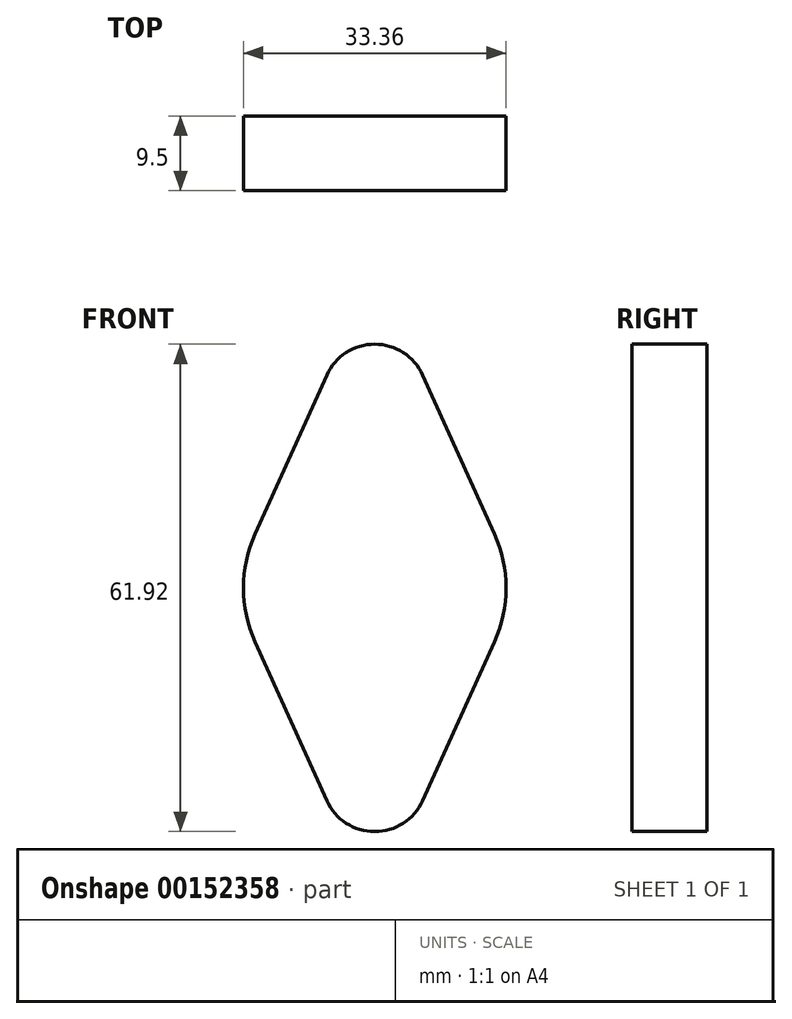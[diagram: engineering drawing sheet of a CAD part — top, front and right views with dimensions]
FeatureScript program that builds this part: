
annotation { "Feature Type Name" : "Feature", "Feature Type Description" : "" }
export const myFeature = defineFeature(function(context is Context, id is Id, definition is map)
    precondition{}
    {
        {
            var Q0;
            Q0=qCreatedBy(makeId("Front.planeOp"),FACE);
            var sketch = newSketch(context, id + "F0", { "sketchPlane" : qUnion([Q0])});
            skArc(sketch, "E0", {"start": v(6.09, 27.03) * mm, "mid": v(0, 30.96) * mm, "end": v(-6.09, 27.03) * mm});
            skArc(sketch, "E1.MirrorC", {"start": v(6.09, -27.03) * mm, "mid": v(0, -30.96) * mm, "end": v(-6.09, -27.03) * mm});
            skArc(sketch, "E2", {"start": v(-15.2, 6.86) * mm, "mid": v(-16.68, 0) * mm, "end": v(-15.2, -6.86) * mm});
            skLineSegment(sketch, "E3", {"start": v(-6.09, 27.03) * mm, "end": v(-15.2, 6.86) * mm});
            skLineSegment(sketch, "E4.MirrorCS", {"start": v(-6.09, -27.03) * mm, "end": v(-15.2, -6.86) * mm});
            skLineSegment(sketch, "E5.MirrorCS", {"start": v(6.09, 27.03) * mm, "end": v(15.2, 6.86) * mm});
            skLineSegment(sketch, "E6.MirrorCS", {"start": v(6.09, -27.03) * mm, "end": v(15.2, -6.86) * mm});
            skArc(sketch, "E7.trimOffspring", {"start": v(15.2, -6.86) * mm, "mid": v(16.68, 0) * mm, "end": v(15.2, 6.86) * mm});
            skCircle(sketch, "E8", {"center": v(0, 24.28) * mm, "radius": 2.8 * mm, "construction": true});
            skCircle(sketch, "E9.MirrorC", {"center": v(0, -24.28) * mm, "radius": 2.8 * mm, "construction": true});
            skSolve(sketch);
        }
        {
            var Q0;
            Q0=makeQuery(id+"F0.imprint","IMPRINT",FACE,{"disambiguationData":[TD([[makeQuery(id+"F0.imprint","IMPRINT",EDGE,{"derivedFrom":sQuery(id+"F0.wireOp",EDGE,"E0")}),1.0]])]});
            extrude(context, id + "F1", {"entities" : qUnion([Q0]), "depth" : 9.5 * mm});
        }
    });
